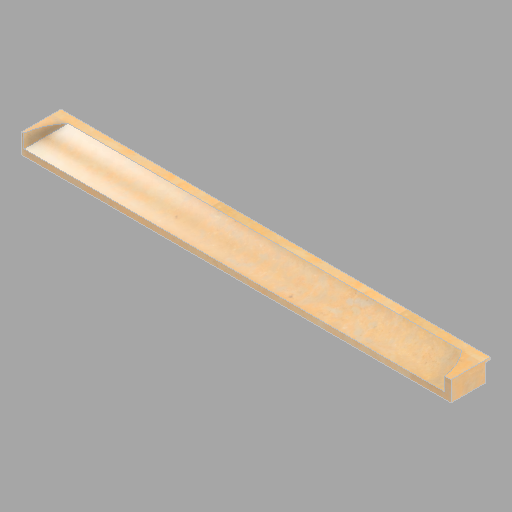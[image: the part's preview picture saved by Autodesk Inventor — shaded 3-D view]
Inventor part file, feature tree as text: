
AUTODESK INVENTOR PART (.ipt)
format: ipt  version: 2022.2 (Build 262287010, 287A)  size: 192,512 bytes
history: native  units: in
note: dims shown in document units (in); Inventor stores cm internally (conversion verified against a paired STEP export)
features: revolve x2, direct_edit x1
ambient origin geometry x8: Origin, YZ Plane, XZ Plane, XY Plane, X Axis, Y Axis, Z Axis, Center Point
bodies: Solid1 (feature_tree), Body1 (feature_tree)
feature tree (3):
  direct_edit  "Direct Edit1"
  revolve  "Rotate1"  Angle=180.0deg
  revolve  "Rotate2"  [1 undecoded]
note: 1 required parameter value undecoded (feature->parameter linkage not recoverable at this tier; creation-order binding heuristic only, values carry confidence <= 0.55)
